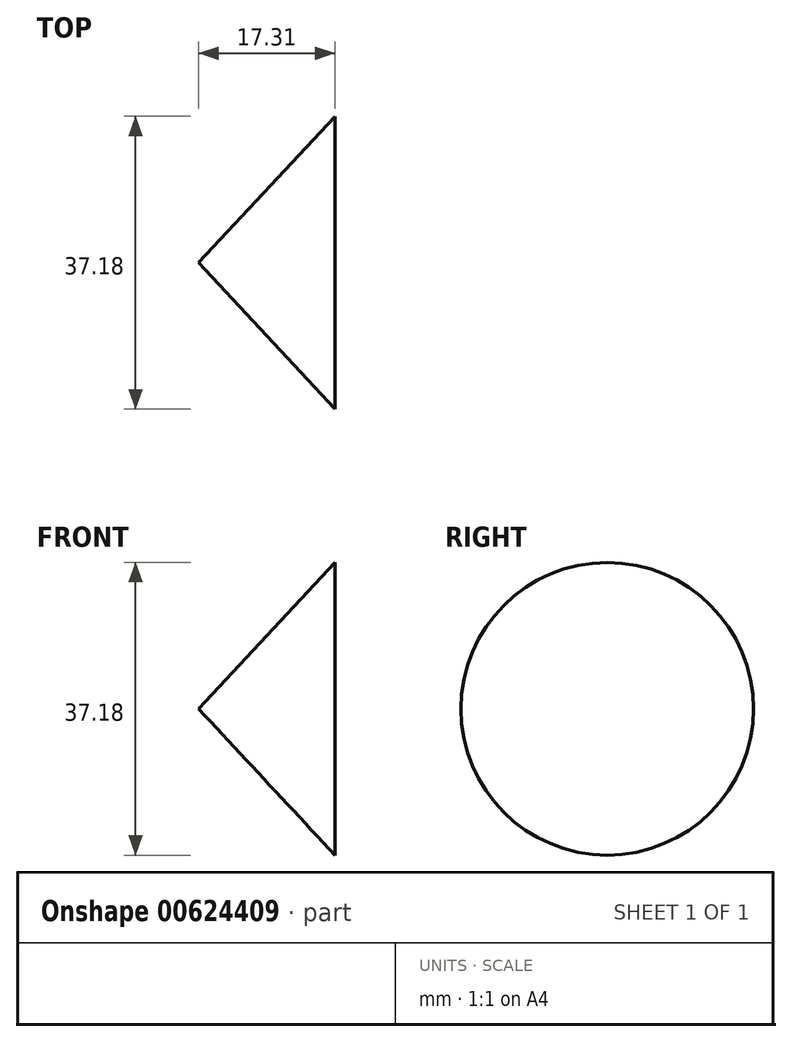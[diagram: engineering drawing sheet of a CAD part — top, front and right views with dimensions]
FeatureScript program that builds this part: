
annotation { "Feature Type Name" : "Feature", "Feature Type Description" : "" }
export const myFeature = defineFeature(function(context is Context, id is Id, definition is map)
    precondition{}
    {
        {
            var Q0;
            Q0=qCreatedBy(makeId("Front.planeOp"),FACE);
            var sketch = newSketch(context, id + "F0", { "sketchPlane" : qUnion([Q0])});
            skLineSegment(sketch, "E0", {"start": v(0, 0) * mm, "end": v(17.31, 18.59) * mm});
            skLineSegment(sketch, "E1", {"start": v(17.31, 18.59) * mm, "end": v(17.31, 0) * mm});
            skLineSegment(sketch, "E2", {"start": v(0, 0) * mm, "end": v(17.31, 0) * mm});
            skSolve(sketch);
        }
        {
            var Q0;
            Q0=makeQuery(id+"F0.imprint","IMPRINT",FACE,{"disambiguationData":[TD([[makeQuery(id+"F0.imprint","IMPRINT",EDGE,{"derivedFrom":sQuery(id+"F0.wireOp",EDGE,"E0")}),-1.0]])]});
            var Q1;
            Q1=sQuery(id+"F0.wireOp",EDGE,"E2");
            revolve(context, id + "F1", {"entities" : qUnion([Q0]), "axis" : qUnion([Q1]), "revolveType" : RevolveType.FULL});
        }
    });
